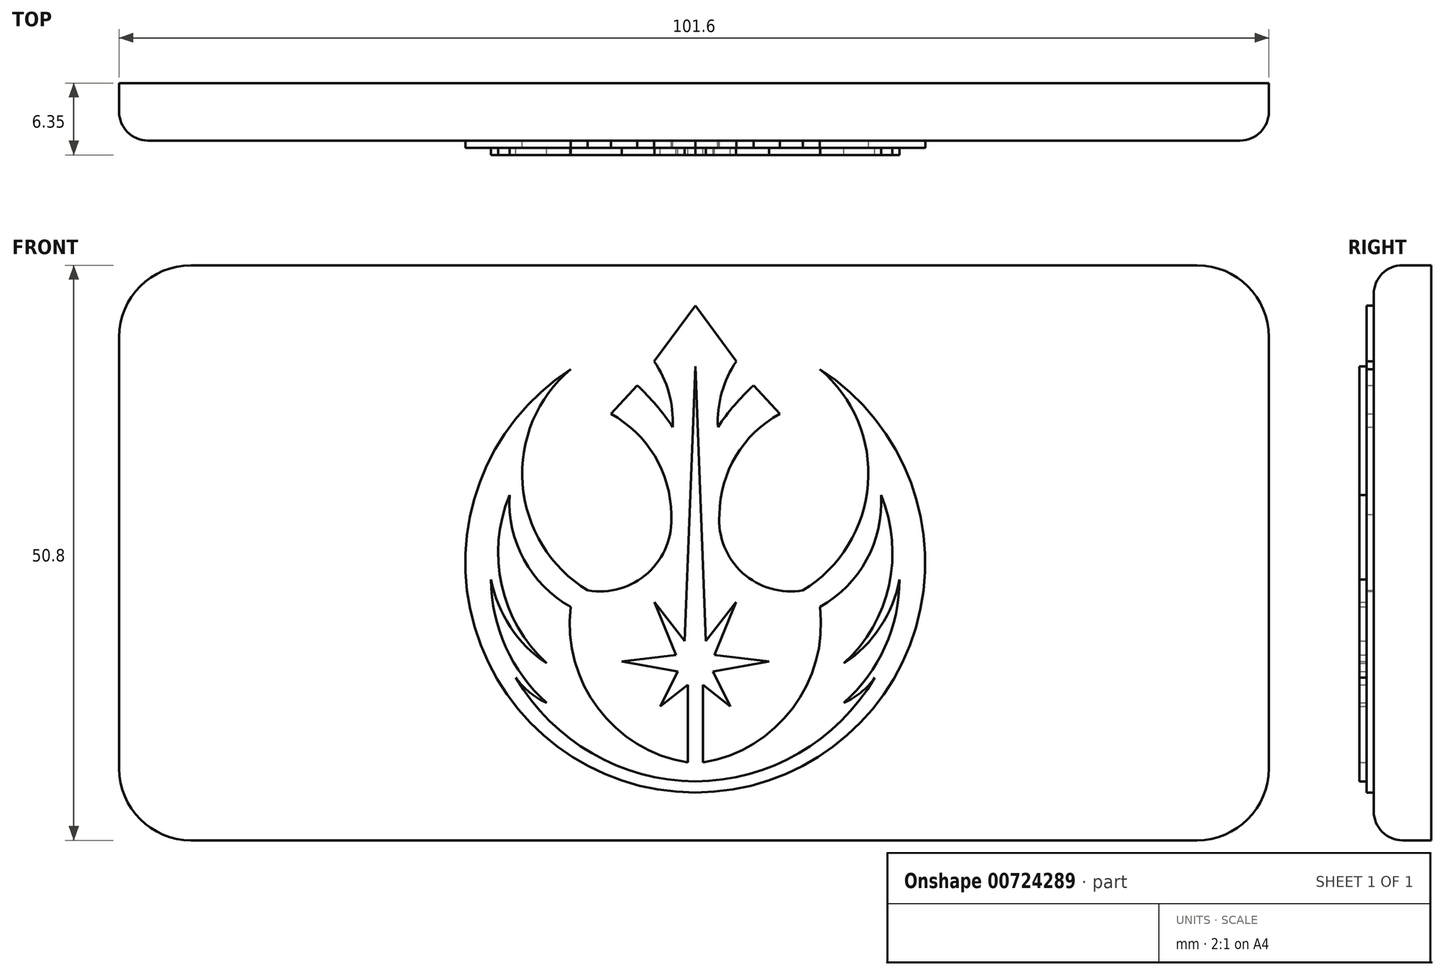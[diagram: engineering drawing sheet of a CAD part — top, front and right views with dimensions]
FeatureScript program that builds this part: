
annotation { "Feature Type Name" : "Feature", "Feature Type Description" : "" }
export const myFeature = defineFeature(function(context is Context, id is Id, definition is map)
    precondition{}
    {
        {
            var Q0;
            Q0=qCreatedBy(makeId("Front.planeOp"),FACE);
            var sketch = newSketch(context, id + "F0", { "sketchPlane" : qUnion([Q0])});
            skLineSegment(sketch, "E0.bottom", {"start": v(-6.35, 0) * mm, "end": v(-95.25, 0) * mm});
            skLineSegment(sketch, "E0.top", {"start": v(-6.35, 50.8) * mm, "end": v(-95.25, 50.8) * mm});
            skLineSegment(sketch, "E0.left", {"start": v(0, 6.35) * mm, "end": v(0, 44.45) * mm});
            skLineSegment(sketch, "E0.right", {"start": v(-101.6, 6.35) * mm, "end": v(-101.6, 44.45) * mm});
            skPoint(sketch, "E1.visualSharp", {"position": v(-101.6, 50.8) * mm});
            skArc(sketch, "E1.filletArc", {"start": v(-95.25, 50.8) * mm, "mid": v(-99.74, 48.94) * mm, "end": v(-101.6, 44.45) * mm});
            skPoint(sketch, "E2.visualSharp", {"position": v(-101.6, 0) * mm});
            skArc(sketch, "E2.filletArc", {"start": v(-101.6, 6.35) * mm, "mid": v(-99.74, 1.86) * mm, "end": v(-95.25, 0) * mm});
            skPoint(sketch, "E3.visualSharp", {"position": v(0, 0) * mm});
            skArc(sketch, "E3.filletArc", {"start": v(-6.35, 0) * mm, "mid": v(-1.86, 1.86) * mm, "end": v(0, 6.35) * mm});
            skPoint(sketch, "E4.visualSharp", {"position": v(0, 50.8) * mm});
            skArc(sketch, "E4.filletArc", {"start": v(0, 44.45) * mm, "mid": v(-1.86, 48.94) * mm, "end": v(-6.35, 50.8) * mm});
            skSolve(sketch);
        }
        {
            var Q0;
            Q0=makeQuery(id+"F0.imprint","IMPRINT",FACE,{"disambiguationData":[TD([[makeQuery(id+"F0.imprint","IMPRINT",EDGE,{"derivedFrom":sQuery(id+"F0.wireOp",EDGE,"E0.bottom")}),-1.0]])]});
            extrude(context, id + "F1", {"entities" : qUnion([Q0]), "depth" : 5.08 * mm, "offsetDistance" : 25.4 * mm});
        }
        {
            var Q0;
            Q0=makeQuery(id+"F1.opExtrude","CAP_EDGE",EDGE,{"disambiguationData":[OSD([sQuery(id+"F0.wireOp",EDGE,"E0.top")])],"isStart":false});
            fillet(context, id + "F2", {"entities" : qUnion([Q0]), "radius" : 2.54 * mm, "tangentPropagation" : true, "allowEdgeOverflow" : false});
        }
        {
            var Q0;
            Q0=makeQuery(id+"F1.opExtrude","CAP_FACE",FACE,{"disambiguationData":[OSD([sQuery(id+"F0.wireOp",EDGE,"E0.bottom"),sQuery(id+"F0.wireOp",EDGE,"E0.top"),sQuery(id+"F0.wireOp",EDGE,"E0.left"),sQuery(id+"F0.wireOp",EDGE,"E0.right"),sQuery(id+"F0.wireOp",EDGE,"E1.filletArc"),sQuery(id+"F0.wireOp",EDGE,"E2.filletArc"),sQuery(id+"F0.wireOp",EDGE,"E3.filletArc"),sQuery(id+"F0.wireOp",EDGE,"E4.filletArc")])],"isStart":false});
            var sketch = newSketch(context, id + "F3", { "sketchPlane" : qUnion([Q0])});
            skArc(sketch, "E5", {"start": v(-61.7, 41.62) * mm, "mid": v(-50.68, 4.22) * mm, "end": v(-39.67, 41.62) * mm});
            skArc(sketch, "E6", {"start": v(-67.1, 30.49) * mm, "mid": v(-65.82, 24.78) * mm, "end": v(-61.7, 20.62) * mm});
            skArc(sketch, "E7", {"start": v(-67.1, 30.49) * mm, "mid": v(-67.8, 22.54) * mm, "end": v(-63.82, 15.63) * mm});
            skArc(sketch, "E8", {"start": v(-68.73, 23.04) * mm, "mid": v(-67.02, 18.84) * mm, "end": v(-63.82, 15.63) * mm});
            skArc(sketch, "E9", {"start": v(-68.73, 23.04) * mm, "mid": v(-67.43, 17.07) * mm, "end": v(-63.82, 12.15) * mm});
            skArc(sketch, "E10", {"start": v(-66.55, 14.37) * mm, "mid": v(-65.33, 13.07) * mm, "end": v(-63.82, 12.15) * mm});
            skArc(sketch, "E11", {"start": v(-66.55, 14.37) * mm, "mid": v(-59.82, 7.69) * mm, "end": v(-50.68, 5.2) * mm});
            skArc(sketch, "E12", {"start": v(-61.7, 20.62) * mm, "mid": v(-59.29, 11.66) * mm, "end": v(-51.35, 6.86) * mm});
            skArc(sketch, "E13", {"start": v(-52.68, 36.5) * mm, "mid": v(-53.02, 39.54) * mm, "end": v(-54.32, 42.3) * mm});
            skArc(sketch, "E14", {"start": v(-52.68, 36.5) * mm, "mid": v(-54.14, 38.44) * mm, "end": v(-55.82, 40.19) * mm});
            skArc(sketch, "E15", {"start": v(-61.7, 41.62) * mm, "mid": v(-65.94, 31.47) * mm, "end": v(-60.2, 22.09) * mm});
            skArc(sketch, "E16", {"start": v(-60.2, 22.09) * mm, "mid": v(-54.86, 23.62) * mm, "end": v(-52.81, 28.78) * mm});
            skArc(sketch, "E17", {"start": v(-52.81, 28.78) * mm, "mid": v(-54.27, 33.95) * mm, "end": v(-58.14, 37.66) * mm});
            skLineSegment(sketch, "E18", {"start": v(-58.14, 37.66) * mm, "end": v(-55.82, 40.19) * mm});
            skLineSegment(sketch, "E19", {"start": v(-54.32, 42.3) * mm, "end": v(-50.68, 47.23) * mm});
            skLineSegment(sketch, "E20", {"start": v(-51.35, 6.86) * mm, "end": v(-51.35, 13.75) * mm});
            skLineSegment(sketch, "E21", {"start": v(-51.35, 13.75) * mm, "end": v(-53.77, 11.84) * mm});
            skLineSegment(sketch, "E22", {"start": v(-53.77, 11.84) * mm, "end": v(-52.24, 14.9) * mm});
            skLineSegment(sketch, "E23", {"start": v(-52.24, 14.9) * mm, "end": v(-57.19, 15.8) * mm});
            skLineSegment(sketch, "E24", {"start": v(-57.19, 15.8) * mm, "end": v(-52.39, 16.36) * mm});
            skLineSegment(sketch, "E25", {"start": v(-52.39, 16.36) * mm, "end": v(-54.28, 21.04) * mm});
            skLineSegment(sketch, "E26", {"start": v(-54.28, 21.04) * mm, "end": v(-51.61, 17.6) * mm});
            skLineSegment(sketch, "E27", {"start": v(-51.61, 17.6) * mm, "end": v(-50.68, 41.85) * mm});
            skLineSegment(sketch, "E28.MirrorCS", {"start": v(-47.05, 42.3) * mm, "end": v(-50.68, 47.23) * mm});
            skArc(sketch, "E29.MirrorCS", {"start": v(-48.69, 36.5) * mm, "mid": v(-47.23, 38.44) * mm, "end": v(-45.55, 40.19) * mm});
            skLineSegment(sketch, "E30.MirrorCS", {"start": v(-43.22, 37.66) * mm, "end": v(-45.55, 40.19) * mm});
            skArc(sketch, "E31.MirrorCS", {"start": v(-48.55, 28.78) * mm, "mid": v(-47.1, 33.95) * mm, "end": v(-43.22, 37.66) * mm});
            skArc(sketch, "E32.MirrorCS", {"start": v(-41.17, 22.09) * mm, "mid": v(-46.5, 23.62) * mm, "end": v(-48.55, 28.78) * mm});
            skArc(sketch, "E33.MirrorCS", {"start": v(-39.67, 41.62) * mm, "mid": v(-35.42, 31.47) * mm, "end": v(-41.17, 22.09) * mm});
            skArc(sketch, "E34.MirrorCS", {"start": v(-34.27, 30.49) * mm, "mid": v(-35.55, 24.78) * mm, "end": v(-39.66, 20.62) * mm});
            skArc(sketch, "E35.MirrorCS", {"start": v(-34.27, 30.49) * mm, "mid": v(-33.57, 22.54) * mm, "end": v(-37.55, 15.63) * mm});
            skArc(sketch, "E36.MirrorCS", {"start": v(-32.63, 23.04) * mm, "mid": v(-34.34, 18.84) * mm, "end": v(-37.55, 15.63) * mm});
            skArc(sketch, "E37.MirrorCS", {"start": v(-32.63, 23.04) * mm, "mid": v(-33.93, 17.07) * mm, "end": v(-37.55, 12.15) * mm});
            skArc(sketch, "E38.MirrorCS", {"start": v(-34.82, 14.37) * mm, "mid": v(-36.03, 13.07) * mm, "end": v(-37.55, 12.15) * mm});
            skArc(sketch, "E39.MirrorCS", {"start": v(-34.82, 14.37) * mm, "mid": v(-41.54, 7.69) * mm, "end": v(-50.68, 5.2) * mm});
            skLineSegment(sketch, "E40.MirrorCS", {"start": v(-50.02, 6.86) * mm, "end": v(-50.02, 13.75) * mm});
            skLineSegment(sketch, "E41.MirrorCS", {"start": v(-50.02, 13.75) * mm, "end": v(-47.6, 11.84) * mm});
            skLineSegment(sketch, "E42.MirrorCS", {"start": v(-47.6, 11.84) * mm, "end": v(-49.13, 14.9) * mm});
            skLineSegment(sketch, "E43.MirrorCS", {"start": v(-49.13, 14.9) * mm, "end": v(-44.18, 15.8) * mm});
            skLineSegment(sketch, "E44.MirrorCS", {"start": v(-44.18, 15.8) * mm, "end": v(-48.98, 16.36) * mm});
            skLineSegment(sketch, "E45.MirrorCS", {"start": v(-48.98, 16.36) * mm, "end": v(-47.08, 21.04) * mm});
            skLineSegment(sketch, "E46.MirrorCS", {"start": v(-47.08, 21.04) * mm, "end": v(-49.75, 17.6) * mm});
            skLineSegment(sketch, "E47.MirrorCS", {"start": v(-49.75, 17.6) * mm, "end": v(-50.68, 41.85) * mm});
            skArc(sketch, "E48.MirrorCS", {"start": v(-48.69, 36.5) * mm, "mid": v(-48.35, 39.54) * mm, "end": v(-47.05, 42.3) * mm});
            skArc(sketch, "E49.MirrorCS", {"start": v(-39.66, 20.62) * mm, "mid": v(-42.08, 11.66) * mm, "end": v(-50.02, 6.86) * mm});
            skSolve(sketch);
        }
        {
            var Q0;
            Q0=makeQuery(id+"F3.imprint","IMPRINT",FACE,{"disambiguationData":[TD([[makeQuery(id+"F3.imprint","IMPRINT",EDGE,{"derivedFrom":sQuery(id+"F3.wireOp",EDGE,"E6")}),-1.0]])]});
            extrude(context, id + "F4", {"entities" : qUnion([Q0]), "operationType" : NewBodyOperationType.ADD, "depth" : 1.27 * mm, "offsetDistance" : 25.4 * mm});
        }
        {
            var Q0;
            Q0=makeQuery(id+"F3.imprint","IMPRINT",FACE,{"disambiguationData":[TD([[makeQuery(id+"F3.imprint","IMPRINT",EDGE,{"derivedFrom":sQuery(id+"F3.wireOp",EDGE,"E5")}),1.0]])]});
            extrude(context, id + "F5", {"entities" : qUnion([Q0]), "operationType" : NewBodyOperationType.ADD, "depth" : 0.64 * mm, "offsetDistance" : 25.4 * mm});
        }
    });
